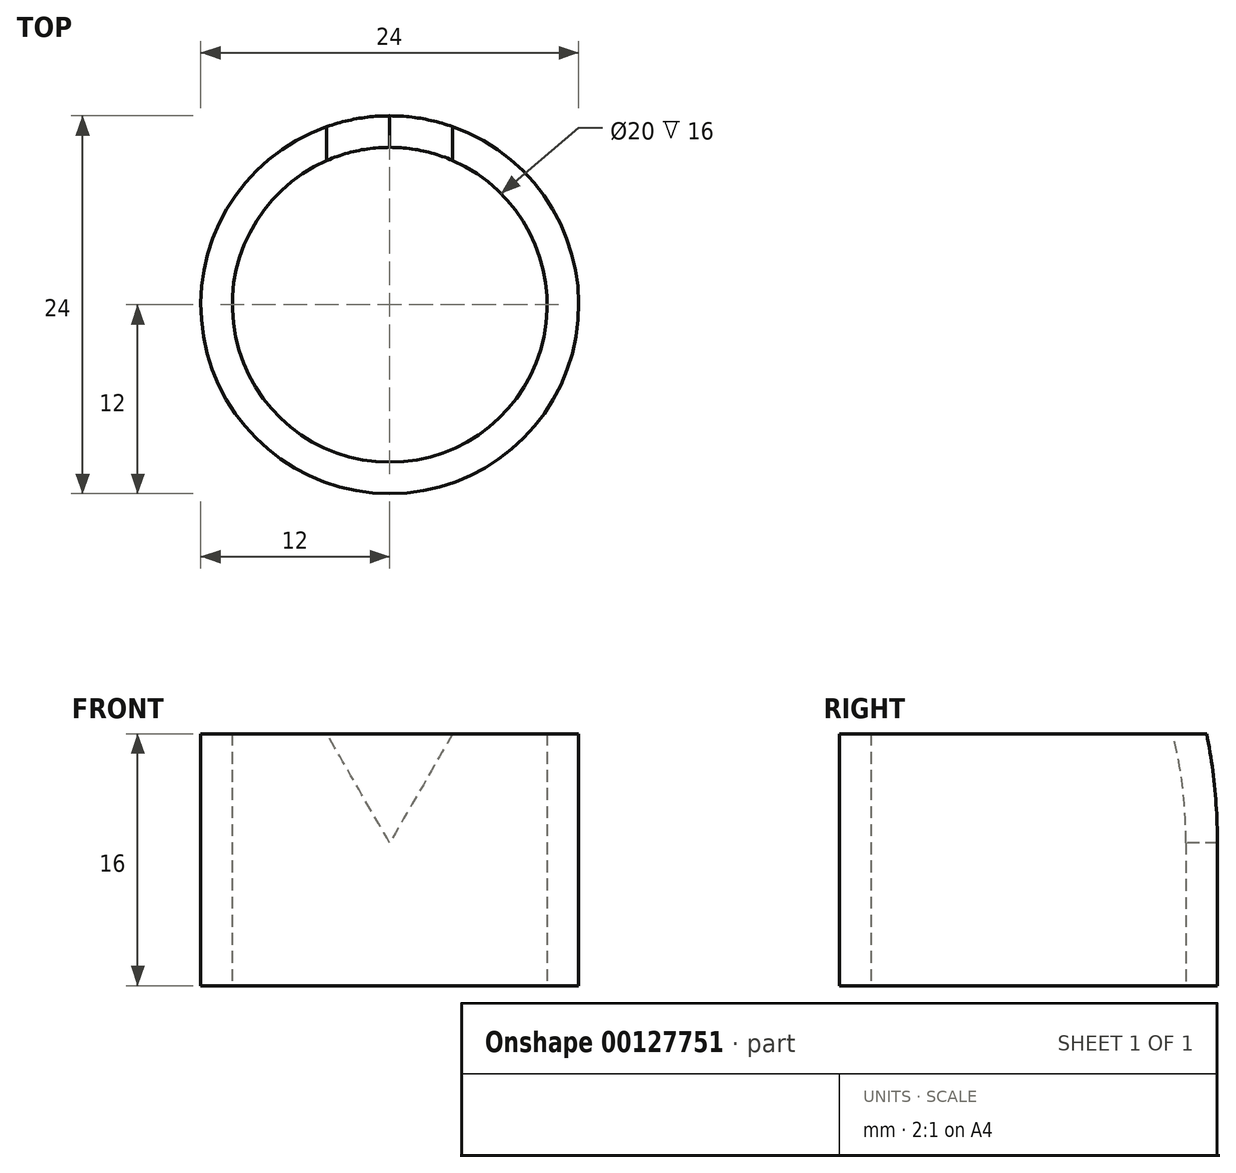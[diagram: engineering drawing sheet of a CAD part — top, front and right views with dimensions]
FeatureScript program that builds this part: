
annotation { "Feature Type Name" : "Feature", "Feature Type Description" : "" }
export const myFeature = defineFeature(function(context is Context, id is Id, definition is map)
    precondition{}
    {
        {
            var Q0;
            Q0=qCreatedBy(makeId("Top.planeOp"),FACE);
            var sketch = newSketch(context, id + "F0", { "sketchPlane" : qUnion([Q0])});
            skCircle(sketch, "E0", {"center": v(0, 0) * mm, "radius": 10 * mm});
            skCircle(sketch, "E1.0", {"center": v(0, 0) * mm, "radius": 12 * mm});
            skSolve(sketch);
        }
        {
            var Q0;
            Q0=makeQuery(id+"F0.imprint","IMPRINT",FACE,{"disambiguationData":[TD([[makeQuery(id+"F0.imprint","IMPRINT",EDGE,{"derivedFrom":sQuery(id+"F0.wireOp",EDGE,"E0")}),-1.0]])]});
            extrude(context, id + "F1", {"entities" : qUnion([Q0]), "depth" : 16 * mm});
        }
        {
            var Q0;
            Q0=qCreatedBy(makeId("Front.planeOp"),FACE);
            var sketch = newSketch(context, id + "F2", { "sketchPlane" : qUnion([Q0])});
            skLineSegment(sketch, "E2.0", {"start": v(-12, 16) * mm, "end": v(12, 16) * mm, "construction": true});
            skLineSegment(sketch, "E3", {"start": v(4, 16) * mm, "end": v(0, 9.07) * mm});
            skLineSegment(sketch, "E4", {"start": v(0, 9.07) * mm, "end": v(-4, 16) * mm});
            skLineSegment(sketch, "E5", {"start": v(-4, 16) * mm, "end": v(4, 16) * mm});
            skSolve(sketch);
        }
        {
            var Q0;
            Q0=makeQuery(id+"F2.imprint","IMPRINT",FACE,{"disambiguationData":[TD([[makeQuery(id+"F2.imprint","IMPRINT",EDGE,{"derivedFrom":sQuery(id+"F2.wireOp",EDGE,"E3")}),-1.0]])]});
            extrude(context, id + "F3", {"entities" : qUnion([Q0]), "operationType" : NewBodyOperationType.REMOVE, "endBound" : BoundingType.THROUGH_ALL, "oppositeDirection" : true, "depth" : 25 * mm});
        }
    });
